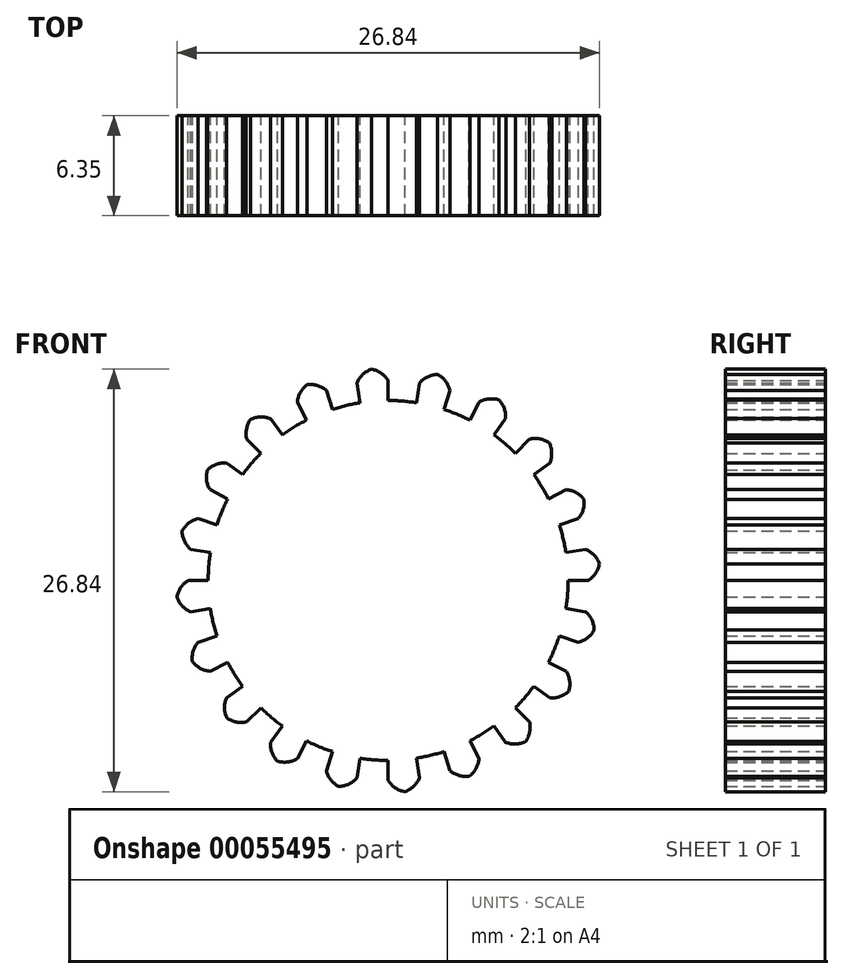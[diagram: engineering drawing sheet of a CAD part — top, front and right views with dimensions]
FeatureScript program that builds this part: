
annotation { "Feature Type Name" : "Feature", "Feature Type Description" : "" }
export const myFeature = defineFeature(function(context is Context, id is Id, definition is map)
    precondition{}
    {
        {
            var Q0;
            Q0=qCreatedBy(makeId("Front.planeOp"),FACE);
            var sketch = newSketch(context, id + "F0", { "sketchPlane" : qUnion([Q0])});
            skArc(sketch, "E0", {"start": v(0, 12.7) * mm, "mid": v(-1, 12.66) * mm, "end": v(-1.99, 12.54) * mm});
            skArc(sketch, "E1", {"start": v(-8.08, 8.08) * mm, "mid": v(-8.7, 7.42) * mm, "end": v(-9.25, 6.72) * mm});
            skLineSegment(sketch, "E2", {"start": v(0, 11.43) * mm, "end": v(0, 12.7) * mm, "construction": true});
            skLineSegment(sketch, "E3", {"start": v(-1.79, 11.29) * mm, "end": v(-1.99, 12.54) * mm, "construction": true});
            skLineSegment(sketch, "E4", {"start": v(-0.9, 11.39) * mm, "end": v(-0.9, 11.4) * mm, "construction": true});
            skArc(sketch, "E5", {"start": v(0, 12.7) * mm, "mid": v(-0.45, 13.17) * mm, "end": v(-1.06, 13.42) * mm});
            skLineSegment(sketch, "E6", {"start": v(0, 12.7) * mm, "end": v(0, 11.43) * mm});
            skPoint(sketch, "E7.orphan", {"position": v(0, 34.16) * mm});
            skPoint(sketch, "E8.orphan", {"position": v(-5.4, 34.16) * mm});
            skArc(sketch, "E9.MirrorCS", {"start": v(-1.99, 12.54) * mm, "mid": v(-1.61, 13.08) * mm, "end": v(-1.06, 13.42) * mm});
            skLineSegment(sketch, "E10.MirrorCS", {"start": v(-1.99, 12.54) * mm, "end": v(-1.79, 11.29) * mm});
            skArc(sketch, "E11.1.0", {"start": v(-5.77, 11.32) * mm, "mid": v(-5.58, 11.94) * mm, "end": v(-5.15, 12.44) * mm});
            skLineSegment(sketch, "E11.1.1", {"start": v(-5.77, 11.32) * mm, "end": v(-5.19, 10.18) * mm});
            skArc(sketch, "E11.1.2", {"start": v(-3.92, 12.08) * mm, "mid": v(-4.5, 12.39) * mm, "end": v(-5.15, 12.44) * mm});
            skLineSegment(sketch, "E11.1.3", {"start": v(-3.92, 12.08) * mm, "end": v(-3.53, 10.87) * mm});
            skArc(sketch, "E11.2.0", {"start": v(-8.98, 8.98) * mm, "mid": v(-9, 9.63) * mm, "end": v(-8.74, 10.24) * mm});
            skLineSegment(sketch, "E11.2.1", {"start": v(-8.98, 8.98) * mm, "end": v(-8.08, 8.08) * mm});
            skArc(sketch, "E11.2.2", {"start": v(-7.46, 10.27) * mm, "mid": v(-8.1, 10.39) * mm, "end": v(-8.74, 10.24) * mm});
            skLineSegment(sketch, "E11.2.3", {"start": v(-7.46, 10.27) * mm, "end": v(-6.72, 9.25) * mm});
            skArc(sketch, "E12.2.3.0", {"start": v(-11.32, 5.77) * mm, "mid": v(-11.53, 6.38) * mm, "end": v(-11.48, 7.03) * mm});
            skLineSegment(sketch, "E12.4.3.0", {"start": v(-11.32, 5.77) * mm, "end": v(-10.18, 5.19) * mm});
            skArc(sketch, "E12.7.3.0", {"start": v(-10.27, 7.46) * mm, "mid": v(-10.92, 7.38) * mm, "end": v(-11.48, 7.03) * mm});
            skLineSegment(sketch, "E12.11.3.0", {"start": v(-10.27, 7.46) * mm, "end": v(-9.25, 6.72) * mm});
            skArc(sketch, "E12.2.4.0", {"start": v(-12.54, 1.99) * mm, "mid": v(-12.94, 2.5) * mm, "end": v(-13.09, 3.14) * mm});
            skLineSegment(sketch, "E12.4.4.0", {"start": v(-12.54, 1.99) * mm, "end": v(-11.29, 1.79) * mm});
            skArc(sketch, "E12.7.4.0", {"start": v(-12.08, 3.92) * mm, "mid": v(-12.67, 3.64) * mm, "end": v(-13.09, 3.14) * mm});
            skLineSegment(sketch, "E12.11.4.0", {"start": v(-12.08, 3.92) * mm, "end": v(-10.87, 3.53) * mm});
            skArc(sketch, "E12.2.5.0", {"start": v(-12.54, -1.99) * mm, "mid": v(-13.08, -1.61) * mm, "end": v(-13.42, -1.06) * mm});
            skLineSegment(sketch, "E12.4.5.0", {"start": v(-12.54, -1.99) * mm, "end": v(-11.29, -1.79) * mm});
            skArc(sketch, "E12.7.5.0", {"start": v(-12.7, 0) * mm, "mid": v(-13.17, -0.45) * mm, "end": v(-13.42, -1.06) * mm});
            skLineSegment(sketch, "E12.11.5.0", {"start": v(-12.7, 0) * mm, "end": v(-11.43, 0) * mm});
            skArc(sketch, "E12.2.6.0", {"start": v(-11.32, -5.77) * mm, "mid": v(-11.94, -5.58) * mm, "end": v(-12.44, -5.15) * mm});
            skLineSegment(sketch, "E12.4.6.0", {"start": v(-11.32, -5.77) * mm, "end": v(-10.18, -5.19) * mm});
            skArc(sketch, "E12.7.6.0", {"start": v(-12.08, -3.92) * mm, "mid": v(-12.39, -4.5) * mm, "end": v(-12.44, -5.15) * mm});
            skLineSegment(sketch, "E12.11.6.0", {"start": v(-12.08, -3.92) * mm, "end": v(-10.87, -3.53) * mm});
            skArc(sketch, "E12.2.7.0", {"start": v(-8.98, -8.98) * mm, "mid": v(-9.63, -9) * mm, "end": v(-10.24, -8.74) * mm});
            skLineSegment(sketch, "E12.4.7.0", {"start": v(-8.98, -8.98) * mm, "end": v(-8.08, -8.08) * mm});
            skArc(sketch, "E12.7.7.0", {"start": v(-10.27, -7.46) * mm, "mid": v(-10.39, -8.1) * mm, "end": v(-10.24, -8.74) * mm});
            skLineSegment(sketch, "E12.11.7.0", {"start": v(-10.27, -7.46) * mm, "end": v(-9.25, -6.72) * mm});
            skArc(sketch, "E12.2.8.0", {"start": v(-5.77, -11.32) * mm, "mid": v(-6.38, -11.53) * mm, "end": v(-7.03, -11.48) * mm});
            skLineSegment(sketch, "E12.4.8.0", {"start": v(-5.77, -11.32) * mm, "end": v(-5.19, -10.18) * mm});
            skArc(sketch, "E12.7.8.0", {"start": v(-7.46, -10.27) * mm, "mid": v(-7.38, -10.92) * mm, "end": v(-7.03, -11.48) * mm});
            skLineSegment(sketch, "E12.11.8.0", {"start": v(-7.46, -10.27) * mm, "end": v(-6.72, -9.25) * mm});
            skArc(sketch, "E12.2.9.0", {"start": v(-1.99, -12.54) * mm, "mid": v(-2.5, -12.94) * mm, "end": v(-3.14, -13.09) * mm});
            skLineSegment(sketch, "E12.4.9.0", {"start": v(-1.99, -12.54) * mm, "end": v(-1.79, -11.29) * mm});
            skArc(sketch, "E12.7.9.0", {"start": v(-3.92, -12.08) * mm, "mid": v(-3.64, -12.67) * mm, "end": v(-3.14, -13.09) * mm});
            skLineSegment(sketch, "E12.11.9.0", {"start": v(-3.92, -12.08) * mm, "end": v(-3.53, -10.87) * mm});
            skArc(sketch, "E12.2.10.0", {"start": v(1.99, -12.54) * mm, "mid": v(1.61, -13.08) * mm, "end": v(1.06, -13.42) * mm});
            skLineSegment(sketch, "E12.4.10.0", {"start": v(1.99, -12.54) * mm, "end": v(1.79, -11.29) * mm});
            skArc(sketch, "E12.7.10.0", {"start": v(0, -12.7) * mm, "mid": v(0.45, -13.17) * mm, "end": v(1.06, -13.42) * mm});
            skLineSegment(sketch, "E12.11.10.0", {"start": v(0, -12.7) * mm, "end": v(0, -11.43) * mm});
            skArc(sketch, "E12.2.11.0", {"start": v(5.77, -11.32) * mm, "mid": v(5.58, -11.94) * mm, "end": v(5.15, -12.44) * mm});
            skLineSegment(sketch, "E12.4.11.0", {"start": v(5.77, -11.32) * mm, "end": v(5.19, -10.18) * mm});
            skArc(sketch, "E12.7.11.0", {"start": v(3.92, -12.08) * mm, "mid": v(4.5, -12.39) * mm, "end": v(5.15, -12.44) * mm});
            skLineSegment(sketch, "E12.11.11.0", {"start": v(3.92, -12.08) * mm, "end": v(3.53, -10.87) * mm});
            skArc(sketch, "E12.2.12.0", {"start": v(8.98, -8.98) * mm, "mid": v(9, -9.63) * mm, "end": v(8.74, -10.24) * mm});
            skLineSegment(sketch, "E12.4.12.0", {"start": v(8.98, -8.98) * mm, "end": v(8.08, -8.08) * mm});
            skArc(sketch, "E12.7.12.0", {"start": v(7.46, -10.27) * mm, "mid": v(8.1, -10.39) * mm, "end": v(8.74, -10.24) * mm});
            skLineSegment(sketch, "E12.11.12.0", {"start": v(7.46, -10.27) * mm, "end": v(6.72, -9.25) * mm});
            skArc(sketch, "E12.2.13.0", {"start": v(11.32, -5.77) * mm, "mid": v(11.53, -6.38) * mm, "end": v(11.48, -7.03) * mm});
            skLineSegment(sketch, "E12.4.13.0", {"start": v(11.32, -5.77) * mm, "end": v(10.18, -5.19) * mm});
            skArc(sketch, "E12.7.13.0", {"start": v(10.27, -7.46) * mm, "mid": v(10.92, -7.38) * mm, "end": v(11.48, -7.03) * mm});
            skLineSegment(sketch, "E12.11.13.0", {"start": v(10.27, -7.46) * mm, "end": v(9.25, -6.72) * mm});
            skArc(sketch, "E12.2.14.0", {"start": v(12.54, -1.99) * mm, "mid": v(12.94, -2.5) * mm, "end": v(13.09, -3.14) * mm});
            skLineSegment(sketch, "E12.4.14.0", {"start": v(12.54, -1.99) * mm, "end": v(11.29, -1.79) * mm});
            skArc(sketch, "E12.7.14.0", {"start": v(12.08, -3.92) * mm, "mid": v(12.67, -3.64) * mm, "end": v(13.09, -3.14) * mm});
            skLineSegment(sketch, "E12.11.14.0", {"start": v(12.08, -3.92) * mm, "end": v(10.87, -3.53) * mm});
            skArc(sketch, "E12.2.15.0", {"start": v(12.54, 1.99) * mm, "mid": v(13.08, 1.61) * mm, "end": v(13.42, 1.06) * mm});
            skLineSegment(sketch, "E12.4.15.0", {"start": v(12.54, 1.99) * mm, "end": v(11.29, 1.79) * mm});
            skArc(sketch, "E12.7.15.0", {"start": v(12.7, 0) * mm, "mid": v(13.17, 0.45) * mm, "end": v(13.42, 1.06) * mm});
            skLineSegment(sketch, "E12.11.15.0", {"start": v(12.7, 0) * mm, "end": v(11.43, 0) * mm});
            skArc(sketch, "E12.2.16.0", {"start": v(11.32, 5.77) * mm, "mid": v(11.94, 5.58) * mm, "end": v(12.44, 5.15) * mm});
            skLineSegment(sketch, "E12.4.16.0", {"start": v(11.32, 5.77) * mm, "end": v(10.18, 5.19) * mm});
            skArc(sketch, "E12.7.16.0", {"start": v(12.08, 3.92) * mm, "mid": v(12.39, 4.5) * mm, "end": v(12.44, 5.15) * mm});
            skLineSegment(sketch, "E12.11.16.0", {"start": v(12.08, 3.92) * mm, "end": v(10.87, 3.53) * mm});
            skArc(sketch, "E12.2.17.0", {"start": v(8.98, 8.98) * mm, "mid": v(9.63, 9) * mm, "end": v(10.24, 8.74) * mm});
            skLineSegment(sketch, "E12.4.17.0", {"start": v(8.98, 8.98) * mm, "end": v(8.08, 8.08) * mm});
            skArc(sketch, "E12.7.17.0", {"start": v(10.27, 7.46) * mm, "mid": v(10.39, 8.1) * mm, "end": v(10.24, 8.74) * mm});
            skLineSegment(sketch, "E12.11.17.0", {"start": v(10.27, 7.46) * mm, "end": v(9.25, 6.72) * mm});
            skArc(sketch, "E12.2.18.0", {"start": v(5.77, 11.32) * mm, "mid": v(6.38, 11.53) * mm, "end": v(7.03, 11.48) * mm});
            skLineSegment(sketch, "E12.4.18.0", {"start": v(5.77, 11.32) * mm, "end": v(5.19, 10.18) * mm});
            skArc(sketch, "E12.7.18.0", {"start": v(7.46, 10.27) * mm, "mid": v(7.38, 10.92) * mm, "end": v(7.03, 11.48) * mm});
            skLineSegment(sketch, "E12.11.18.0", {"start": v(7.46, 10.27) * mm, "end": v(6.72, 9.25) * mm});
            skArc(sketch, "E12.2.19.0", {"start": v(1.99, 12.54) * mm, "mid": v(2.5, 12.94) * mm, "end": v(3.14, 13.09) * mm});
            skLineSegment(sketch, "E12.4.19.0", {"start": v(1.99, 12.54) * mm, "end": v(1.79, 11.29) * mm});
            skArc(sketch, "E12.7.19.0", {"start": v(3.92, 12.08) * mm, "mid": v(3.64, 12.67) * mm, "end": v(3.14, 13.09) * mm});
            skLineSegment(sketch, "E12.11.19.0", {"start": v(3.92, 12.08) * mm, "end": v(3.53, 10.87) * mm});
            skArc(sketch, "E13.trimOffspring", {"start": v(-10.18, 5.19) * mm, "mid": v(-10.56, 4.37) * mm, "end": v(-10.87, 3.53) * mm});
            skArc(sketch, "E14.trimOffspring", {"start": v(-11.29, 1.79) * mm, "mid": v(-11.4, 0.9) * mm, "end": v(-11.43, 0) * mm});
            skArc(sketch, "E15.trimOffspring", {"start": v(-11.29, -1.79) * mm, "mid": v(-11.11, -2.67) * mm, "end": v(-10.87, -3.53) * mm});
            skArc(sketch, "E16.trimOffspring", {"start": v(-10.18, -5.19) * mm, "mid": v(-9.75, -5.97) * mm, "end": v(-9.25, -6.72) * mm});
            skArc(sketch, "E17.trimOffspring", {"start": v(-5.19, 10.18) * mm, "mid": v(-5.97, 9.75) * mm, "end": v(-6.72, 9.25) * mm});
            skArc(sketch, "E18.trimOffspring", {"start": v(-1.79, 11.29) * mm, "mid": v(-2.67, 11.11) * mm, "end": v(-3.53, 10.87) * mm});
            skArc(sketch, "E19.trimOffspring", {"start": v(1.79, 11.29) * mm, "mid": v(0.9, 11.4) * mm, "end": v(0, 11.43) * mm});
            skArc(sketch, "E20.trimOffspring", {"start": v(5.19, 10.18) * mm, "mid": v(4.37, 10.56) * mm, "end": v(3.53, 10.87) * mm});
            skArc(sketch, "E21.trimOffspring", {"start": v(8.08, 8.08) * mm, "mid": v(7.42, 8.7) * mm, "end": v(6.72, 9.25) * mm});
            skArc(sketch, "E22.trimOffspring", {"start": v(10.18, 5.19) * mm, "mid": v(9.75, 5.97) * mm, "end": v(9.25, 6.72) * mm});
            skArc(sketch, "E23.trimOffspring", {"start": v(11.29, 1.79) * mm, "mid": v(11.11, 2.67) * mm, "end": v(10.87, 3.53) * mm});
            skArc(sketch, "E24.trimOffspring", {"start": v(11.29, -1.79) * mm, "mid": v(11.4, -0.9) * mm, "end": v(11.43, 0) * mm});
            skArc(sketch, "E25.trimOffspring", {"start": v(10.18, -5.19) * mm, "mid": v(10.56, -4.37) * mm, "end": v(10.87, -3.53) * mm});
            skArc(sketch, "E26.trimOffspring", {"start": v(8.08, -8.08) * mm, "mid": v(8.7, -7.42) * mm, "end": v(9.25, -6.72) * mm});
            skArc(sketch, "E27.trimOffspring", {"start": v(5.19, -10.18) * mm, "mid": v(5.97, -9.75) * mm, "end": v(6.72, -9.25) * mm});
            skArc(sketch, "E28.trimOffspring", {"start": v(1.79, -11.29) * mm, "mid": v(2.67, -11.11) * mm, "end": v(3.53, -10.87) * mm});
            skArc(sketch, "E29.trimOffspring", {"start": v(-1.79, -11.29) * mm, "mid": v(-0.9, -11.4) * mm, "end": v(0, -11.43) * mm});
            skArc(sketch, "E30.trimOffspring", {"start": v(-5.19, -10.18) * mm, "mid": v(-4.37, -10.56) * mm, "end": v(-3.53, -10.87) * mm});
            skArc(sketch, "E31.trimOffspring", {"start": v(-8.08, -8.08) * mm, "mid": v(-7.42, -8.7) * mm, "end": v(-6.72, -9.25) * mm});
            skSolve(sketch);
        }
        {
            var Q0;
            Q0 = qSketchRegion(id + "F0", true);
            extrude(context, id + "F1", {"entities" : qUnion([Q0]), "depth" : 6.35 * mm});
        }
    });
